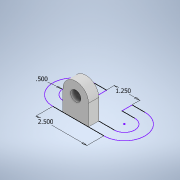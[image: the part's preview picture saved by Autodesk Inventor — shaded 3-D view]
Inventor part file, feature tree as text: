
AUTODESK INVENTOR PART (.ipt)
format: ipt  version: 2022.2 (Build 262287030, 287C)  size: 119,296 bytes
history: native  units: in
note: dims shown in document units (in); Inventor stores cm internally (conversion verified against a paired STEP export)
features: sketch x2, extrude x1, projected_geometry x1
ambient origin geometry x8: Origin, YZ Plane, XZ Plane, XY Plane, X Axis, Y Axis, Z Axis, Center Point
bodies: Solid1 (feature_tree)
feature tree (4):
  extrude  "Extrusion1"  Depth=0.625in
  sketch  "Sketch3"  dims[d2=0.5in d4=0.5in d5=0.0in d6=2.5in d7=0.5in d9=1.25in]
  sketch  "Sketch2"  dims[d0=0.625in d1=1.0in]
  projected_geometry  "Projected Loop1"
